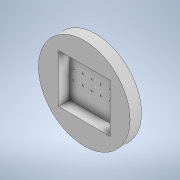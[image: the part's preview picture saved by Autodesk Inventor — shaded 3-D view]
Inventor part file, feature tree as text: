
AUTODESK INVENTOR PART (.ipt)
format: ipt  version: 2021 (Build 250183000, 183)  size: 305,664 bytes
history: native  units: in
note: dims shown in document units (in); Inventor stores cm internally (conversion verified against a paired STEP export)
features: sketch x6, extrude x5, projected_geometry x4, pattern_linear x2, plane x1, mirror x1
ambient origin geometry x8: Origin, YZ Plane, XZ Plane, XY Plane, X Axis, Y Axis, Z Axis, Center Point
bodies: Body1 (feature_tree)
feature tree (19):
  sketch  "Sketch1"  dims[d0=1.1295in d1=1.06in]
  plane  "Work Plane1"
  extrude  "Extrusion2"  Depth=1.06in
  extrude  "Extrusion3"  Depth=0.25in TaperAngle=0.0deg
  extrude  "Extrusion4"  Depth=0.006in TaperAngle=0.0deg
  pattern_linear  "Rectangular Pattern1"  Count1=12 Spacing1=0.1in
  extrude  "Extrusion5"  Depth=0.006in TaperAngle=0.0deg
  extrude  "Extrusion6"  TaperAngle=0.0deg  [1 undecoded]
  pattern_linear  "Rectangular Pattern2"  Count1=6 Spacing1=0.2in
  mirror  "Mirror1"
  sketch  "Sketch6"
  sketch  "Sketch2"  dims[d4=2.0in d5=0.25in d6=0.0in]
  sketch  "Sketch3"  dims[d7=0.25in d8=0.0in d10=0.006in d11=0.0in d12=4.7244in d14=0.1in]
  projected_geometry  "Projected Loop1"
  projected_geometry  "Projected Loop2"
  sketch  "Sketch4"  dims[d15=0.01in d16=0.006in d17=0.0in]
  projected_geometry  "Projected Loop3"
  sketch  "Sketch5"  dims[d18=0.0394in d20=0.0in d21=0.0in d22=2.3622in d24=0.2in]
  projected_geometry  "Projected Loop4"
note: 1 required parameter value undecoded (feature->parameter linkage not recoverable at this tier; creation-order binding heuristic only, values carry confidence <= 0.55)
